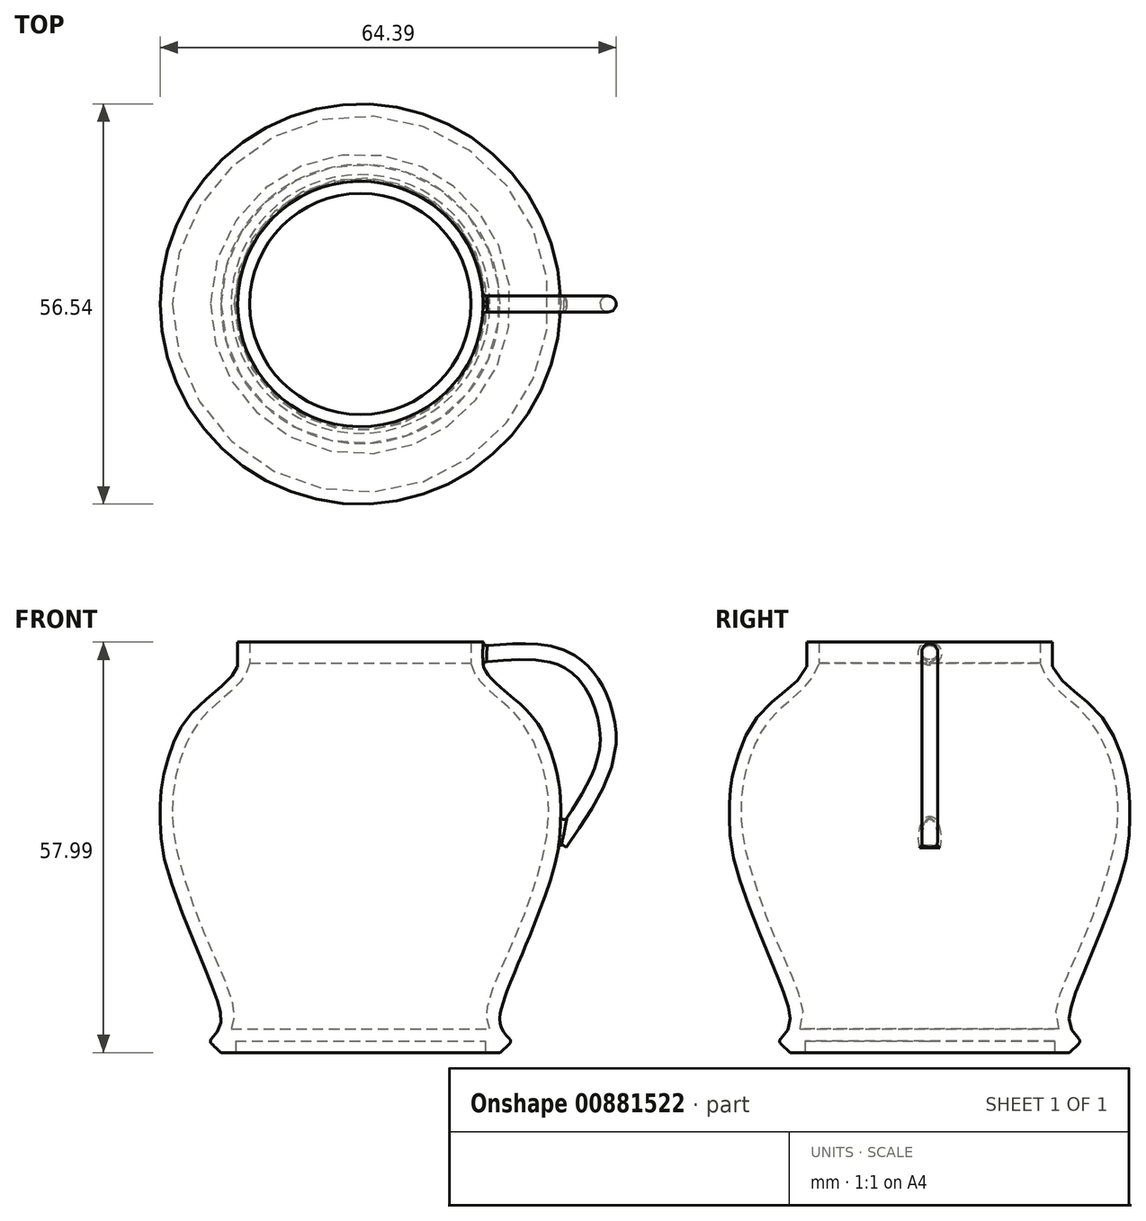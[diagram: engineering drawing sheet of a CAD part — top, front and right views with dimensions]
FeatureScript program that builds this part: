
annotation { "Feature Type Name" : "Feature", "Feature Type Description" : "" }
export const myFeature = defineFeature(function(context is Context, id is Id, definition is map)
    precondition{}
    {
        {
            var Q0;
            Q0=qCreatedBy(makeId("Front.planeOp"),FACE);
            var sketch = newSketch(context, id + "F0", { "sketchPlane" : qUnion([Q0])});
            skLineSegment(sketch, "E0", {"start": v(59.22, 12.73) * mm, "end": v(59.22, 70.72) * mm});
            skLineSegment(sketch, "E1", {"start": v(59.22, 14.35) * mm, "end": v(76.85, 14.35) * mm});
            skLineSegment(sketch, "E2", {"start": v(76.85, 14.35) * mm, "end": v(76.85, 12.73) * mm});
            skLineSegment(sketch, "E3", {"start": v(76.85, 12.73) * mm, "end": v(78.92, 12.73) * mm});
            skLineSegment(sketch, "E4", {"start": v(78.92, 12.73) * mm, "end": v(80.63, 14.35) * mm});
            skFitSpline(sketch, "E5", {"points": [v(80.63, 14.35) * mm, v(79.55, 15.48) * mm, v(78.92, 17.1) * mm, v(79.25, 19.43) * mm, v(81.14, 24.46) * mm, v(86.74, 39.45) * mm, v(87.49, 46.2) * mm, v(87.24, 50.82) * mm, v(85.81, 56) * mm, v(83.02, 60.74) * mm, v(77.84, 65.4) * mm, v(76.56, 67.3) * mm], "startDerivative": vector(-22.37, 19.95) * mm, "endDerivative": vector(-13.9, 28.16) * mm});
            skLineSegment(sketch, "E6", {"start": v(76.56, 67.3) * mm, "end": v(76.56, 70.72) * mm});
            skLineSegment(sketch, "E7", {"start": v(76.56, 70.72) * mm, "end": v(74.85, 70.72) * mm});
            skLineSegment(sketch, "E8", {"start": v(74.85, 70.72) * mm, "end": v(74.85, 67.73) * mm});
            skFitSpline(sketch, "E9", {"points": [v(74.85, 67.73) * mm, v(75.46, 66.19) * mm, v(77.33, 63.92) * mm, v(80.03, 61.62) * mm, v(82.22, 59.14) * mm, v(83.98, 55.97) * mm, v(85.55, 50.42) * mm, v(85.55, 43.33) * mm, v(83.82, 36.47) * mm, v(80.8, 28.41) * mm, v(77.11, 18.92) * mm, v(77.49, 16.05) * mm], "startDerivative": vector(8.56, -28.11) * mm, "endDerivative": vector(11.8, -34.53) * mm});
            skLineSegment(sketch, "E10", {"start": v(77.49, 16.05) * mm, "end": v(59.22, 16.05) * mm});
            skSolve(sketch);
        }
        {
            var Q0;
            Q0 = qSketchRegion(id + "F0", true);
            var Q1;
            Q1=sQuery(id+"F0.wireOp",EDGE,"E0");
            revolve(context, id + "F1", {"surfaceOperationType" : NewSurfaceOperationType.NEW, "entities" : qUnion([Q0]), "axis" : qUnion([Q1]), "revolveType" : RevolveType.FULL});
        }
        {
            var Q0;
            Q0=qCreatedBy(makeId("Front.planeOp"),FACE);
            var sketch = newSketch(context, id + "F2", { "sketchPlane" : qUnion([Q0])});
            skFitSpline(sketch, "E11", {"points": [v(76.19, 69.02) * mm, v(85.88, 69.06) * mm, v(90.3, 66.79) * mm, v(92.9, 62.93) * mm, v(94.01, 55.03) * mm, v(87.33, 42.39) * mm], "startDerivative": vector(46.93, 3.74) * mm, "endDerivative": vector(-33.26, -48.22) * mm});
            skSolve(sketch);
        }
        {
            var Q0;
            Q0=sQuery(id+"F2.wireOp",VERTEX,"E11.end");
            var Q1;
            Q1=sQuery(id+"F2.wireOp",EDGE,"E11");
            cPlane(context, id + "F3", {"entities" : qUnion([Q0, Q1]), "cplaneType" : CPlaneType.CURVE_POINT, "offset" : 25 * mm, "width" : 150 * mm, "height" : 150 * mm});
        }
        {
            var Q0;
            Q0=qCreatedBy(id+"F3.planeOp",FACE);
            var sketch = newSketch(context, id + "F4", { "sketchPlane" : qUnion([Q0])});
            skCircle(sketch, "E12", {"center": v(47.84, 0) * mm, "radius": 1.13 * mm});
            skSolve(sketch);
        }
        {
            var Q0;
            Q0 = qSketchRegion(id + "F4", true);
            var Q1;
            Q1=sQuery(id+"F2.wireOp",EDGE,"E11");
            sweep(context, id + "F5", {"operationType" : NewBodyOperationType.ADD, "profiles" : qUnion([Q0]), "path" : qUnion([Q1])});
        }
        {
            var Q0;
            Q0=makeQuery(id+"F5.boolean.opBoolean","INTERSECT",EDGE,{"derivedFrom":[makeQuery(id+"F1.opRevolve","SWEPT_FACE",FACE,{"disambiguationData":[OSD([sQuery(id+"F0.wireOp",EDGE,"E5")])]}),makeQuery(id+"F5.opSweep","SWEPT_FACE",FACE,{"disambiguationData":[OSD([sQuery(id+"F2.wireOp",EDGE,"E11"),sQuery(id+"F4.wireOp",EDGE,"E12")])]})]});
            var Q1;
            Q1=makeQuery(id+"F1.opRevolve","SWEPT_FACE",FACE,{"disambiguationData":[OSD([sQuery(id+"F0.wireOp",EDGE,"E5")])]});
            fillet(context, id + "F6", {"entities" : qUnion([Q0, Q1]), "radius" : 0.47 * mm, "tangentPropagation" : true, "allowEdgeOverflow" : false});
        }
        {
            var Q0;
            Q0=makeQuery(id+"F5.boolean.opBoolean","INTERSECT",EDGE,{"derivedFrom":[makeQuery(id+"F1.opRevolve","SWEPT_FACE",FACE,{"disambiguationData":[OSD([sQuery(id+"F0.wireOp",EDGE,"E6")])]}),makeQuery(id+"F5.opSweep","SWEPT_FACE",FACE,{"disambiguationData":[OSD([sQuery(id+"F2.wireOp",EDGE,"E11"),sQuery(id+"F4.wireOp",EDGE,"E12")])]})]});
            fillet(context, id + "F7", {"entities" : qUnion([Q0]), "radius" : 0.56 * mm, "tangentPropagation" : true, "allowEdgeOverflow" : false});
        }
    });
